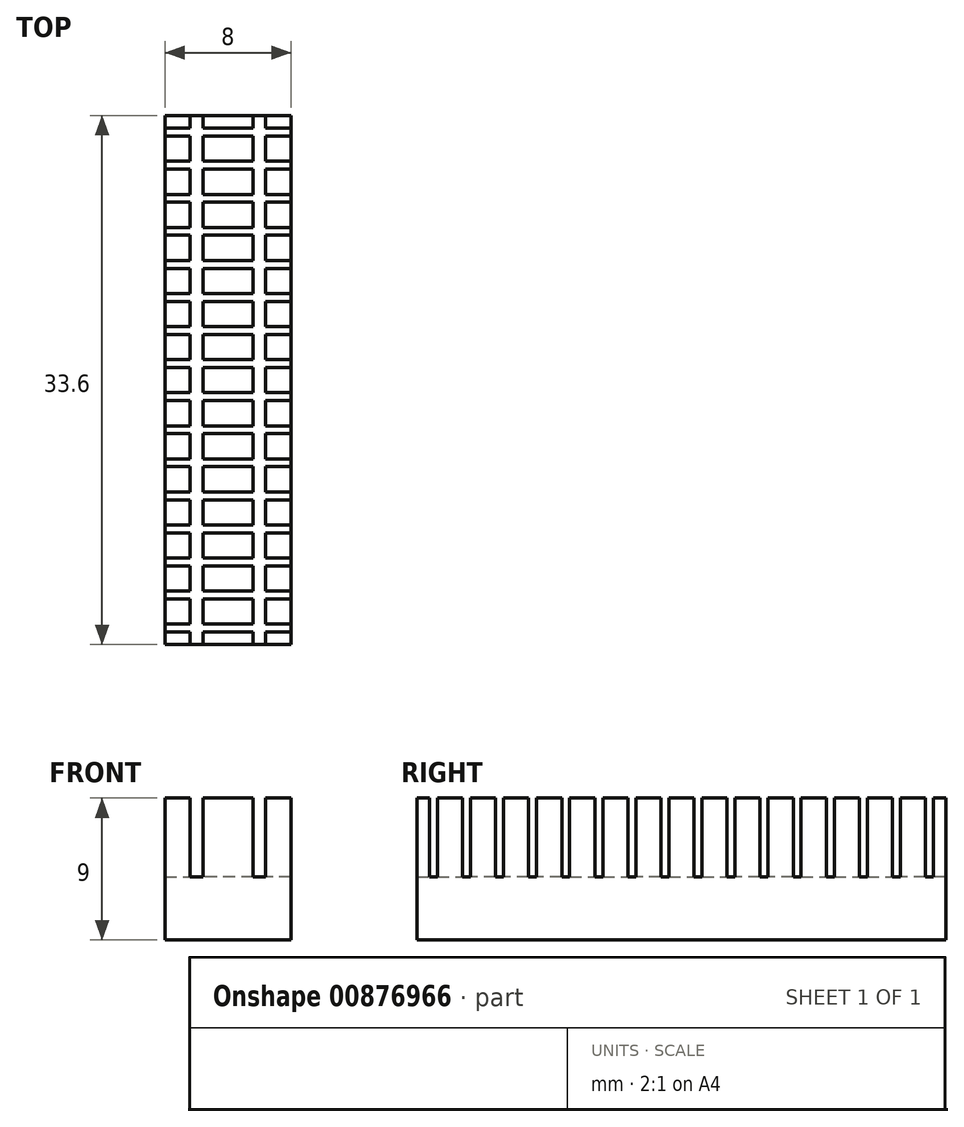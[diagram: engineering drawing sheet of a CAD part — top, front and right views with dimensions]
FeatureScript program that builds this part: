
annotation { "Feature Type Name" : "Feature", "Feature Type Description" : "" }
export const myFeature = defineFeature(function(context is Context, id is Id, definition is map)
    precondition{}
    {
        {
            var Q0;
            Q0=qCreatedBy(makeId("Top.planeOp"),FACE);
            var sketch = newSketch(context, id + "F0", { "sketchPlane" : qUnion([Q0])});
            skLineSegment(sketch, "E0.bottom", {"start": v(2, 1.05) * mm, "end": v(-2, 1.05) * mm});
            skLineSegment(sketch, "E0.top", {"start": v(2, -1.05) * mm, "end": v(-2, -1.05) * mm});
            skLineSegment(sketch, "E0.left", {"start": v(2, 1.05) * mm, "end": v(2, -1.05) * mm});
            skLineSegment(sketch, "E0.right", {"start": v(-2, 1.05) * mm, "end": v(-2, -1.05) * mm});
            skPoint(sketch, "E0.middle", {"position": v(0, 0) * mm});
            skLineSegment(sketch, "E1.bottom", {"start": v(2, 0.25) * mm, "end": v(-2, 0.25) * mm});
            skLineSegment(sketch, "E1.top", {"start": v(2, -0.25) * mm, "end": v(-2, -0.25) * mm});
            skLineSegment(sketch, "E1.left", {"start": v(2, 0.25) * mm, "end": v(2, -0.25) * mm});
            skLineSegment(sketch, "E1.right", {"start": v(-2, 0.25) * mm, "end": v(-2, -0.25) * mm});
            skLineSegment(sketch, "E2.bottom", {"start": v(0.4, 1.05) * mm, "end": v(-0.4, 1.05) * mm});
            skLineSegment(sketch, "E2.top", {"start": v(0.4, -1.05) * mm, "end": v(-0.4, -1.05) * mm});
            skLineSegment(sketch, "E2.left", {"start": v(0.4, 1.05) * mm, "end": v(0.4, -1.05) * mm});
            skLineSegment(sketch, "E2.right", {"start": v(-0.4, 1.05) * mm, "end": v(-0.4, -1.05) * mm});
            skSolve(sketch);
        }
        {
            var Q0;
            {var subQ0=sQuery(id+"F0.wireOp",EDGE,"E0.left");var subQ1=sQuery(id+"F0.wireOp",EDGE,"E0.top");var subQ2=makeQuery(id+"F0.imprint","INTERSECT",VERTEX,{"derivedFrom":[subQ1,subQ0]});Q0=makeQuery(id+"F0.imprint","IMPRINT",FACE,{"disambiguationData":[TD([[makeQuery(id+"F0.imprint","IMPRINT",EDGE,{"disambiguationData":[TD([[subQ2,-1.0]])],"derivedFrom":subQ1}),-1.0]])]});}
            var Q1;
            {var subQ0=sQuery(id+"F0.wireOp",EDGE,"E2.right");var subQ1=sQuery(id+"F0.wireOp",EDGE,"E0.bottom");var subQ2=makeQuery(id+"F0.imprint","INTERSECT",VERTEX,{"derivedFrom":[subQ1,subQ0]});Q1=makeQuery(id+"F0.imprint","IMPRINT",FACE,{"disambiguationData":[TD([[makeQuery(id+"F0.imprint","IMPRINT",EDGE,{"disambiguationData":[TD([[subQ2,1.0]])],"derivedFrom":subQ1}),1.0]])]});}
            var Q2;
            {var subQ0=sQuery(id+"F0.wireOp",EDGE,"E1.top");var subQ1=sQuery(id+"F0.wireOp",EDGE,"E0.left");var subQ2=makeQuery(id+"F0.imprint","INTERSECT",VERTEX,{"derivedFrom":[subQ1,subQ0]});Q2=makeQuery(id+"F0.imprint","IMPRINT",FACE,{"disambiguationData":[TD([[makeQuery(id+"F0.imprint","IMPRINT",EDGE,{"disambiguationData":[TD([[subQ2,1.0]])],"derivedFrom":subQ1}),-1.0]])]});}
            var Q3;
            {var subQ0=sQuery(id+"F0.wireOp",EDGE,"E2.right");var subQ1=sQuery(id+"F0.wireOp",EDGE,"E0.top");var subQ2=makeQuery(id+"F0.imprint","INTERSECT",VERTEX,{"derivedFrom":[subQ1,subQ0]});Q3=makeQuery(id+"F0.imprint","IMPRINT",FACE,{"disambiguationData":[TD([[makeQuery(id+"F0.imprint","IMPRINT",EDGE,{"disambiguationData":[TD([[subQ2,1.0]])],"derivedFrom":subQ1}),-1.0]])]});}
            var Q4;
            {var subQ0=sQuery(id+"F0.wireOp",EDGE,"E2.right");var subQ1=sQuery(id+"F0.wireOp",EDGE,"E0.top");var subQ2=makeQuery(id+"F0.imprint","INTERSECT",VERTEX,{"derivedFrom":[subQ1,subQ0]});Q4=makeQuery(id+"F0.imprint","IMPRINT",FACE,{"disambiguationData":[TD([[makeQuery(id+"F0.imprint","IMPRINT",EDGE,{"disambiguationData":[TD([[subQ2,-1.0]])],"derivedFrom":subQ1}),-1.0]])]});}
            var Q5;
            {var subQ0=sQuery(id+"F0.wireOp",EDGE,"E2.right");var subQ1=sQuery(id+"F0.wireOp",EDGE,"E0.bottom");var subQ2=makeQuery(id+"F0.imprint","INTERSECT",VERTEX,{"derivedFrom":[subQ1,subQ0]});Q5=makeQuery(id+"F0.imprint","IMPRINT",FACE,{"disambiguationData":[TD([[makeQuery(id+"F0.imprint","IMPRINT",EDGE,{"disambiguationData":[TD([[subQ2,-1.0]])],"derivedFrom":subQ1}),1.0]])]});}
            var Q6;
            {var subQ0=sQuery(id+"F0.wireOp",EDGE,"E0.left");var subQ1=sQuery(id+"F0.wireOp",EDGE,"E0.bottom");var subQ2=makeQuery(id+"F0.imprint","INTERSECT",VERTEX,{"derivedFrom":[subQ1,subQ0]});Q6=makeQuery(id+"F0.imprint","IMPRINT",FACE,{"disambiguationData":[TD([[makeQuery(id+"F0.imprint","IMPRINT",EDGE,{"disambiguationData":[TD([[subQ2,-1.0]])],"derivedFrom":subQ1}),1.0]])]});}
            var Q7;
            {var subQ0=sQuery(id+"F0.wireOp",EDGE,"E1.top");var subQ1=sQuery(id+"F0.wireOp",EDGE,"E0.right");var subQ2=makeQuery(id+"F0.imprint","INTERSECT",VERTEX,{"derivedFrom":[subQ1,subQ0]});Q7=makeQuery(id+"F0.imprint","IMPRINT",FACE,{"disambiguationData":[TD([[makeQuery(id+"F0.imprint","IMPRINT",EDGE,{"disambiguationData":[TD([[subQ2,1.0]])],"derivedFrom":subQ1}),1.0]])]});}
            var Q8;
            {var subQ0=sQuery(id+"F0.wireOp",EDGE,"E2.right");var subQ1=sQuery(id+"F0.wireOp",EDGE,"E1.bottom");var subQ2=makeQuery(id+"F0.imprint","INTERSECT",VERTEX,{"derivedFrom":[subQ1,subQ0]});Q8=makeQuery(id+"F0.imprint","IMPRINT",FACE,{"disambiguationData":[TD([[makeQuery(id+"F0.imprint","IMPRINT",EDGE,{"disambiguationData":[TD([[subQ2,1.0]])],"derivedFrom":subQ1}),1.0]])]});}
            extrude(context, id + "F1", {"entities" : qUnion([Q0, Q1, Q2, Q3, Q4, Q5, Q6, Q7, Q8]), "oppositeDirection" : true, "depth" : 4 * mm, "offsetDistance" : 25 * mm});
        }
        {
            var Q0;
            {var subQ0=sQuery(id+"F0.wireOp",EDGE,"E0.left");var subQ1=sQuery(id+"F0.wireOp",EDGE,"E0.bottom");var subQ2=makeQuery(id+"F0.imprint","INTERSECT",VERTEX,{"derivedFrom":[subQ1,subQ0]});Q0=makeQuery(id+"F0.imprint","IMPRINT",FACE,{"disambiguationData":[TD([[makeQuery(id+"F0.imprint","IMPRINT",EDGE,{"disambiguationData":[TD([[subQ2,-1.0]])],"derivedFrom":subQ1}),1.0]])]});}
            var Q1;
            {var subQ0=sQuery(id+"F0.wireOp",EDGE,"E2.right");var subQ1=sQuery(id+"F0.wireOp",EDGE,"E0.bottom");var subQ2=makeQuery(id+"F0.imprint","INTERSECT",VERTEX,{"derivedFrom":[subQ1,subQ0]});Q1=makeQuery(id+"F0.imprint","IMPRINT",FACE,{"disambiguationData":[TD([[makeQuery(id+"F0.imprint","IMPRINT",EDGE,{"disambiguationData":[TD([[subQ2,-1.0]])],"derivedFrom":subQ1}),1.0]])]});}
            var Q2;
            {var subQ0=sQuery(id+"F0.wireOp",EDGE,"E0.left");var subQ1=sQuery(id+"F0.wireOp",EDGE,"E0.top");var subQ2=makeQuery(id+"F0.imprint","INTERSECT",VERTEX,{"derivedFrom":[subQ1,subQ0]});Q2=makeQuery(id+"F0.imprint","IMPRINT",FACE,{"disambiguationData":[TD([[makeQuery(id+"F0.imprint","IMPRINT",EDGE,{"disambiguationData":[TD([[subQ2,-1.0]])],"derivedFrom":subQ1}),-1.0]])]});}
            var Q3;
            {var subQ0=sQuery(id+"F0.wireOp",EDGE,"E2.right");var subQ1=sQuery(id+"F0.wireOp",EDGE,"E0.top");var subQ2=makeQuery(id+"F0.imprint","INTERSECT",VERTEX,{"derivedFrom":[subQ1,subQ0]});Q3=makeQuery(id+"F0.imprint","IMPRINT",FACE,{"disambiguationData":[TD([[makeQuery(id+"F0.imprint","IMPRINT",EDGE,{"disambiguationData":[TD([[subQ2,-1.0]])],"derivedFrom":subQ1}),-1.0]])]});}
            extrude(context, id + "F2", {"entities" : qUnion([Q0, Q1, Q2, Q3]), "operationType" : NewBodyOperationType.ADD, "depth" : 5 * mm, "offsetDistance" : 25 * mm});
        }
        {
            var Q0;
            Q0=makeQuery(id+"F1.opExtrude","SWEPT_BODY",BODY,{"disambiguationData":[OSD([sQuery(id+"F0.wireOp",EDGE,"E0.bottom"),sQuery(id+"F0.wireOp",EDGE,"E0.top"),sQuery(id+"F0.wireOp",EDGE,"E0.left"),sQuery(id+"F0.wireOp",EDGE,"E0.right")])]});
            var Q1;
            {var subQ0=sQuery(id+"F0.wireOp",EDGE,"E0.top");Q1=makeQuery(id+"F2.boolean.opBoolean","MERGE",FACE,{"derivedFrom":[makeQuery(id+"F1.opExtrude","SWEPT_FACE",FACE,{"disambiguationData":[OSD([subQ0])]}),makeQuery(id+"F2.opExtrude","SWEPT_FACE",FACE,{"disambiguationData":[OSD([subQ0]),TDD([makeQuery(id+"F0.imprint","IMPRINT",EDGE,{"disambiguationData":[TD([[makeQuery(id+"F0.imprint","INTERSECT",VERTEX,{"derivedFrom":[subQ0,sQuery(id+"F0.wireOp",EDGE,"E2.right")]}),-1.0]])],"derivedFrom":subQ0})])]}),makeQuery(id+"F2.opExtrude","SWEPT_FACE",FACE,{"disambiguationData":[OSD([subQ0]),TDD([makeQuery(id+"F0.imprint","IMPRINT",EDGE,{"disambiguationData":[TD([[makeQuery(id+"F0.imprint","INTERSECT",VERTEX,{"derivedFrom":[subQ0,sQuery(id+"F0.wireOp",EDGE,"E0.left")]}),-1.0]])],"derivedFrom":subQ0})])]})]});}
            mirror(context, id + "F3", {"operationType" : NewBodyOperationType.ADD, "entities" : qUnion([Q0]), "mirrorPlane" : qUnion([Q1])});
        }
        {
            var Q0;
            Q0=makeQuery(id+"F1.opExtrude","SWEPT_BODY",BODY,{"disambiguationData":[OSD([sQuery(id+"F0.wireOp",EDGE,"E0.bottom"),sQuery(id+"F0.wireOp",EDGE,"E0.top"),sQuery(id+"F0.wireOp",EDGE,"E0.left"),sQuery(id+"F0.wireOp",EDGE,"E0.right")])]});
            var Q1;
            {var subQ0=sQuery(id+"F0.wireOp",EDGE,"E0.bottom");Q1=makeQuery(id+"F3.opPattern","COPY",FACE,{"derivedFrom":makeQuery(id+"F2.boolean.opBoolean","MERGE",FACE,{"derivedFrom":[makeQuery(id+"F1.opExtrude","SWEPT_FACE",FACE,{"disambiguationData":[OSD([subQ0])]}),makeQuery(id+"F2.opExtrude","SWEPT_FACE",FACE,{"disambiguationData":[OSD([subQ0]),TDD([makeQuery(id+"F0.imprint","IMPRINT",EDGE,{"disambiguationData":[TD([[makeQuery(id+"F0.imprint","INTERSECT",VERTEX,{"derivedFrom":[subQ0,sQuery(id+"F0.wireOp",EDGE,"E2.right")]}),-1.0]])],"derivedFrom":subQ0})])]}),makeQuery(id+"F2.opExtrude","SWEPT_FACE",FACE,{"disambiguationData":[OSD([subQ0]),TDD([makeQuery(id+"F0.imprint","IMPRINT",EDGE,{"disambiguationData":[TD([[makeQuery(id+"F0.imprint","INTERSECT",VERTEX,{"derivedFrom":[subQ0,sQuery(id+"F0.wireOp",EDGE,"E0.left")]}),-1.0]])],"derivedFrom":subQ0})])]})]}),"instanceName":"1"});}
            mirror(context, id + "F4", {"operationType" : NewBodyOperationType.ADD, "entities" : qUnion([Q0]), "mirrorPlane" : qUnion([Q1])});
        }
        {
            var Q0;
            Q0=makeQuery(id+"F1.opExtrude","SWEPT_BODY",BODY,{"disambiguationData":[OSD([sQuery(id+"F0.wireOp",EDGE,"E0.bottom"),sQuery(id+"F0.wireOp",EDGE,"E0.top"),sQuery(id+"F0.wireOp",EDGE,"E0.left"),sQuery(id+"F0.wireOp",EDGE,"E0.right")])]});
            var Q1;
            {var subQ0=sQuery(id+"F0.wireOp",EDGE,"E0.bottom");Q1=makeQuery(id+"F4.opPattern","COPY",FACE,{"derivedFrom":makeQuery(id+"F2.boolean.opBoolean","MERGE",FACE,{"derivedFrom":[makeQuery(id+"F1.opExtrude","SWEPT_FACE",FACE,{"disambiguationData":[OSD([subQ0])]}),makeQuery(id+"F2.opExtrude","SWEPT_FACE",FACE,{"disambiguationData":[OSD([subQ0]),TDD([makeQuery(id+"F0.imprint","IMPRINT",EDGE,{"disambiguationData":[TD([[makeQuery(id+"F0.imprint","INTERSECT",VERTEX,{"derivedFrom":[subQ0,sQuery(id+"F0.wireOp",EDGE,"E2.right")]}),-1.0]])],"derivedFrom":subQ0})])]}),makeQuery(id+"F2.opExtrude","SWEPT_FACE",FACE,{"disambiguationData":[OSD([subQ0]),TDD([makeQuery(id+"F0.imprint","IMPRINT",EDGE,{"disambiguationData":[TD([[makeQuery(id+"F0.imprint","INTERSECT",VERTEX,{"derivedFrom":[subQ0,sQuery(id+"F0.wireOp",EDGE,"E0.left")]}),-1.0]])],"derivedFrom":subQ0})])]})]}),"instanceName":"1"});}
            mirror(context, id + "F5", {"operationType" : NewBodyOperationType.ADD, "entities" : qUnion([Q0]), "mirrorPlane" : qUnion([Q1])});
        }
        {
            var Q0;
            Q0=makeQuery(id+"F1.opExtrude","SWEPT_BODY",BODY,{"disambiguationData":[OSD([sQuery(id+"F0.wireOp",EDGE,"E0.bottom"),sQuery(id+"F0.wireOp",EDGE,"E0.top"),sQuery(id+"F0.wireOp",EDGE,"E0.left"),sQuery(id+"F0.wireOp",EDGE,"E0.right")])]});
            var Q1;
            {var subQ0=sQuery(id+"F0.wireOp",EDGE,"E0.bottom");Q1=makeQuery(id+"F5.opPattern","COPY",FACE,{"derivedFrom":makeQuery(id+"F2.boolean.opBoolean","MERGE",FACE,{"derivedFrom":[makeQuery(id+"F1.opExtrude","SWEPT_FACE",FACE,{"disambiguationData":[OSD([subQ0])]}),makeQuery(id+"F2.opExtrude","SWEPT_FACE",FACE,{"disambiguationData":[OSD([subQ0]),TDD([makeQuery(id+"F0.imprint","IMPRINT",EDGE,{"disambiguationData":[TD([[makeQuery(id+"F0.imprint","INTERSECT",VERTEX,{"derivedFrom":[subQ0,sQuery(id+"F0.wireOp",EDGE,"E2.right")]}),-1.0]])],"derivedFrom":subQ0})])]}),makeQuery(id+"F2.opExtrude","SWEPT_FACE",FACE,{"disambiguationData":[OSD([subQ0]),TDD([makeQuery(id+"F0.imprint","IMPRINT",EDGE,{"disambiguationData":[TD([[makeQuery(id+"F0.imprint","INTERSECT",VERTEX,{"derivedFrom":[subQ0,sQuery(id+"F0.wireOp",EDGE,"E0.left")]}),-1.0]])],"derivedFrom":subQ0})])]})]}),"instanceName":"1"});}
            mirror(context, id + "F6", {"operationType" : NewBodyOperationType.ADD, "entities" : qUnion([Q0]), "mirrorPlane" : qUnion([Q1])});
        }
        {
            var Q0;
            Q0=makeQuery(id+"F1.opExtrude","SWEPT_BODY",BODY,{"disambiguationData":[OSD([sQuery(id+"F0.wireOp",EDGE,"E0.bottom"),sQuery(id+"F0.wireOp",EDGE,"E0.top"),sQuery(id+"F0.wireOp",EDGE,"E0.left"),sQuery(id+"F0.wireOp",EDGE,"E0.right")])]});
            var Q1;
            {var subQ0=sQuery(id+"F0.wireOp",EDGE,"E0.right");var subQ1=makeQuery(id+"F2.boolean.opBoolean","MERGE",FACE,{"derivedFrom":[makeQuery(id+"F1.opExtrude","SWEPT_FACE",FACE,{"disambiguationData":[OSD([subQ0])]}),makeQuery(id+"F2.opExtrude","SWEPT_FACE",FACE,{"disambiguationData":[OSD([subQ0]),TDD([makeQuery(id+"F0.imprint","IMPRINT",EDGE,{"disambiguationData":[TD([[makeQuery(id+"F0.imprint","INTERSECT",VERTEX,{"derivedFrom":[subQ0,sQuery(id+"F0.wireOp",EDGE,"E1.top")]}),-1.0]])],"derivedFrom":subQ0})])]}),makeQuery(id+"F2.opExtrude","SWEPT_FACE",FACE,{"disambiguationData":[OSD([subQ0]),TDD([makeQuery(id+"F0.imprint","IMPRINT",EDGE,{"disambiguationData":[TD([[makeQuery(id+"F0.imprint","INTERSECT",VERTEX,{"derivedFrom":[sQuery(id+"F0.wireOp",EDGE,"E0.bottom"),subQ0]}),-1.0]])],"derivedFrom":subQ0})])]})]});var subQ2=makeQuery(id+"F3.boolean.opBoolean","MERGE",FACE,{"derivedFrom":[subQ1,makeQuery(id+"F3.opPattern","COPY",FACE,{"derivedFrom":subQ1,"instanceName":"1"})]});var subQ3=makeQuery(id+"F4.boolean.opBoolean","MERGE",FACE,{"derivedFrom":[subQ2,makeQuery(id+"F4.opPattern","COPY",FACE,{"derivedFrom":subQ2,"instanceName":"1"})]});var subQ4=makeQuery(id+"F5.boolean.opBoolean","MERGE",FACE,{"derivedFrom":[subQ3,makeQuery(id+"F5.opPattern","COPY",FACE,{"derivedFrom":subQ3,"instanceName":"1"})]});Q1=makeQuery(id+"F6.boolean.opBoolean","MERGE",FACE,{"derivedFrom":[subQ4,makeQuery(id+"F6.opPattern","COPY",FACE,{"derivedFrom":subQ4,"instanceName":"1"})]});}
            mirror(context, id + "F7", {"operationType" : NewBodyOperationType.ADD, "entities" : qUnion([Q0]), "mirrorPlane" : qUnion([Q1])});
        }
    });
